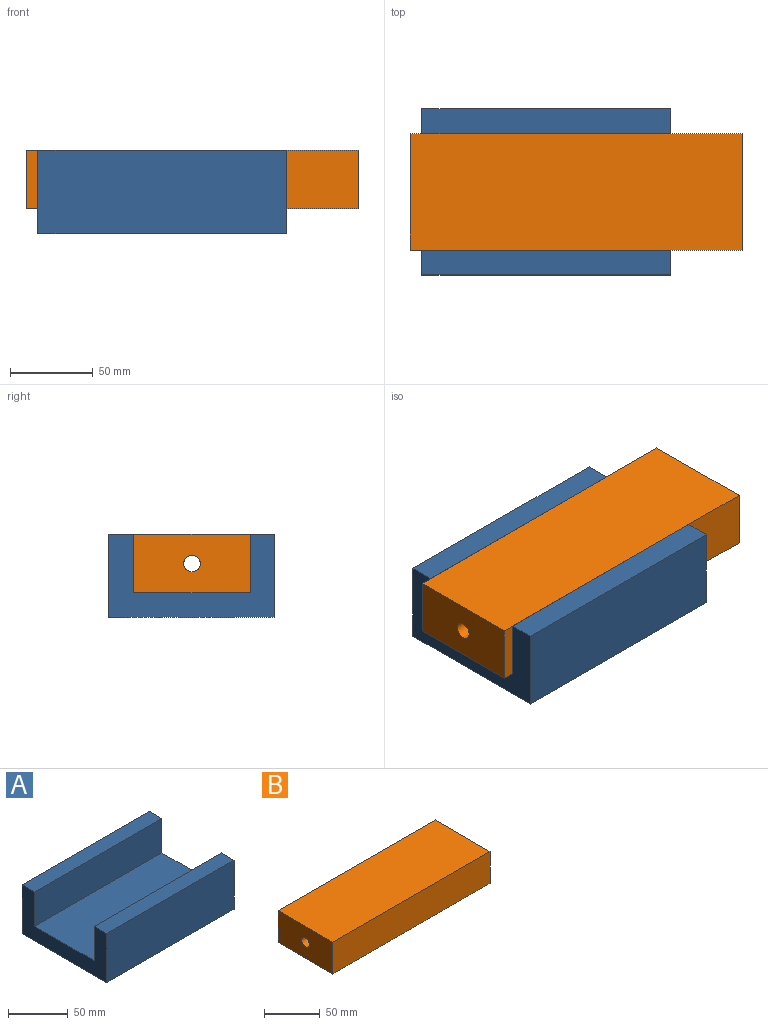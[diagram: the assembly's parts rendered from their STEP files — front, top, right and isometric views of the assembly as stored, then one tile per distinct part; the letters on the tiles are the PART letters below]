
ASSEMBLY  parts=2 mates=2
PART A: 10 faces, bbox 150x100x50 mm
  f0: plane 150x15mm, normal (0,0,1), area 2250mm2, adj f1,f2,f4,f9
  f1: plane 100x50mm, normal (-1,0,0), area 2550mm2, adj f0,f3,f4,f5,f6,f7,f8,f9
  f2: plane 100x50mm, normal (1,0,0), area 2550mm2, adj f0,f3,f4,f5,f6,f7,f8,f9
  f3: plane 150x50mm, normal (0,-1,0), area 7500mm2, adj f1,f2,f5,f6
  f4: plane 150x50mm, normal (0,1,0), area 7500mm2, adj f0,f1,f2,f6
  f5: plane 150x15mm, normal (0,0,1), area 2250mm2, adj f1,f2,f3,f7
  f6: plane 150x100mm, normal (0,0,-1), area 15000mm2, adj f1,f2,f3,f4
  f7: plane 150x35mm, normal (0,1,0), area 5250mm2, adj f1,f2,f5,f8
  f8: plane 150x70mm, normal (0,0,1), area 10500mm2, adj f1,f2,f7,f9
  f9: plane 150x35mm, normal (0,-1,0), area 5250mm2, adj f0,f1,f2,f8
PART B: 7 faces, bbox 200x70x35 mm
  f0: plane 70x35mm, normal (-1,0,0), area 2371.5mm2, adj f1,f3,f4,f5,f6
  f1: plane 200x35mm, normal (0,-1,0), area 7000mm2, adj f0,f2,f4,f5
  f2: plane 70x35mm, normal (1,0,0), area 2371.5mm2, adj f1,f3,f4,f5,f6
  f3: plane 200x35mm, normal (0,1,0), area 7000mm2, adj f0,f2,f4,f5
  f4: plane 200x70mm, normal (0,0,1), area 14000mm2, adj f0,f1,f2,f3
  f5: plane 200x70mm, normal (0,0,-1), area 14000mm2, adj f0,f1,f2,f3
  f6: cylinder r=5mm len=200mm, axis (1,0,0), area 6283.2mm2, adj f0,f2
PLACE A t=(-18.66,7.33,47.07)mm fixed
PLACE B t=(-25.85,22.33,62.07)mm
MATE planar B.f5 <-> A.f8  axis (0,0,-1) through (74.15,57.33,62.07)mm
MATE planar B.f1 <-> A.f7  axis (0,-1,0) through (74.15,22.33,97.07)mm
